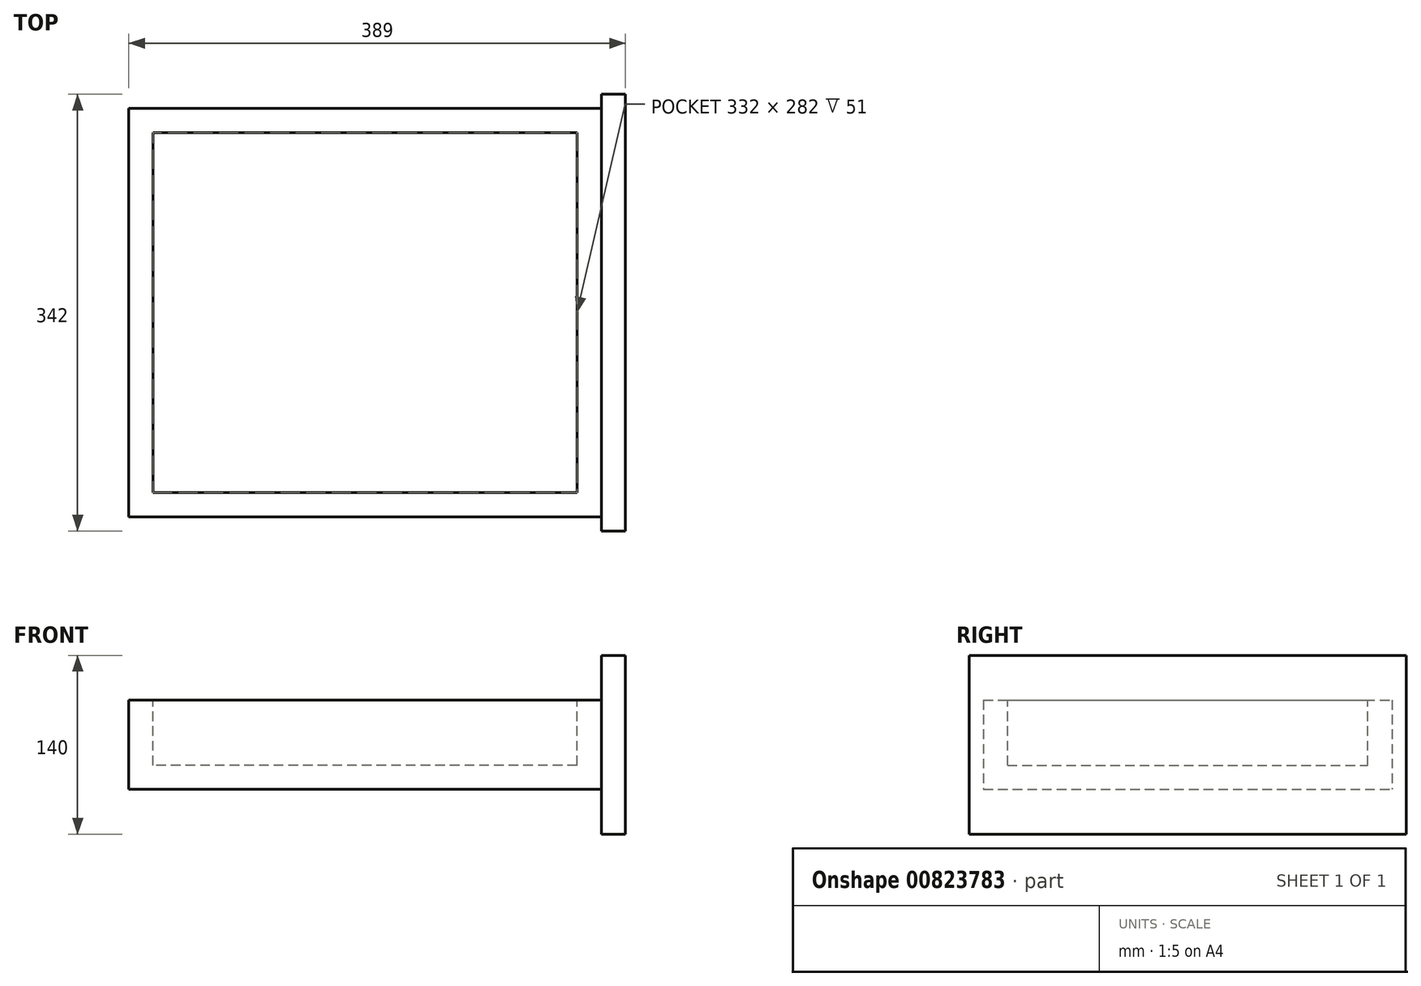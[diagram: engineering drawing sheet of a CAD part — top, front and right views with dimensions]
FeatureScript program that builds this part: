
annotation { "Feature Type Name" : "Feature", "Feature Type Description" : "" }
export const myFeature = defineFeature(function(context is Context, id is Id, definition is map)
    precondition{}
    {
        {
            var Q0;
            Q0=qCreatedBy(makeId("Top.planeOp"),FACE);
            var sketch = newSketch(context, id + "F0", { "sketchPlane" : qUnion([Q0])});
            skLineSegment(sketch, "E0.bottom", {"start": v(185, -160) * mm, "end": v(-185, -160) * mm});
            skLineSegment(sketch, "E0.top", {"start": v(185, 160) * mm, "end": v(-185, 160) * mm});
            skLineSegment(sketch, "E0.left", {"start": v(185, -160) * mm, "end": v(185, 160) * mm});
            skLineSegment(sketch, "E0.right", {"start": v(-185, -160) * mm, "end": v(-185, 160) * mm});
            skPoint(sketch, "E0.middle", {"position": v(0, 0) * mm});
            skSolve(sketch);
        }
        {
            var Q0;
            Q0=makeQuery(id+"F0.imprint","IMPRINT",FACE,{"disambiguationData":[TD([[makeQuery(id+"F0.imprint","IMPRINT",EDGE,{"derivedFrom":sQuery(id+"F0.wireOp",EDGE,"E0.bottom")}),-1.0]])]});
            extrude(context, id + "F1", {"entities" : qUnion([Q0]), "depth" : 70 * mm, "offsetDistance" : 25 * mm});
        }
        {
            var Q0;
            Q0=makeQuery(id+"F1.opExtrude","CAP_FACE",FACE,{"disambiguationData":[OSD([sQuery(id+"F0.wireOp",EDGE,"E0.bottom"),sQuery(id+"F0.wireOp",EDGE,"E0.top"),sQuery(id+"F0.wireOp",EDGE,"E0.left"),sQuery(id+"F0.wireOp",EDGE,"E0.right")])],"isStart":false});
            var sketch = newSketch(context, id + "F2", { "sketchPlane" : qUnion([Q0])});
            skLineSegment(sketch, "E1.bottom", {"start": v(166, -141) * mm, "end": v(-166, -141) * mm});
            skLineSegment(sketch, "E1.top", {"start": v(166, 141) * mm, "end": v(-166, 141) * mm});
            skLineSegment(sketch, "E1.left", {"start": v(166, -141) * mm, "end": v(166, 141) * mm});
            skLineSegment(sketch, "E1.right", {"start": v(-166, -141) * mm, "end": v(-166, 141) * mm});
            skPoint(sketch, "E1.middle", {"position": v(0, 0) * mm});
            skSolve(sketch);
        }
        {
            var Q0;
            Q0=makeQuery(id+"F2.imprint","IMPRINT",FACE,{"disambiguationData":[TD([[makeQuery(id+"F2.imprint","IMPRINT",EDGE,{"derivedFrom":sQuery(id+"F2.wireOp",EDGE,"E1.bottom")}),-1.0]])]});
            extrude(context, id + "F3", {"entities" : qUnion([Q0]), "operationType" : NewBodyOperationType.REMOVE, "oppositeDirection" : true, "depth" : 51 * mm, "offsetDistance" : 25 * mm});
        }
        {
            var Q0;
            Q0=makeQuery(id+"F1.opExtrude","SWEPT_FACE",FACE,{"disambiguationData":[OSD([sQuery(id+"F0.wireOp",EDGE,"E0.left")])]});
            var sketch = newSketch(context, id + "F4", { "sketchPlane" : qUnion([Q0])});
            skLineSegment(sketch, "E2.bottom", {"start": v(171, -35) * mm, "end": v(-171, -35) * mm});
            skLineSegment(sketch, "E2.top", {"start": v(171, 105) * mm, "end": v(-171, 105) * mm});
            skLineSegment(sketch, "E2.left", {"start": v(171, -35) * mm, "end": v(171, 105) * mm});
            skLineSegment(sketch, "E2.right", {"start": v(-171, -35) * mm, "end": v(-171, 105) * mm});
            skPoint(sketch, "E2.middle", {"position": v(0, 35) * mm});
            skPoint(sketch, "E2.middle.positionSnap0", {"position": v(-160, 35) * mm});
            skPoint(sketch, "E2.centerSnap0", {"position": v(-160, 35) * mm});
            skSolve(sketch);
        }
        {
            var Q0;
            Q0 = qSketchRegion(id + "F4", true);
            extrude(context, id + "F5", {"entities" : qUnion([Q0]), "operationType" : NewBodyOperationType.ADD, "depth" : 19 * mm, "offsetDistance" : 25 * mm});
        }
    });
